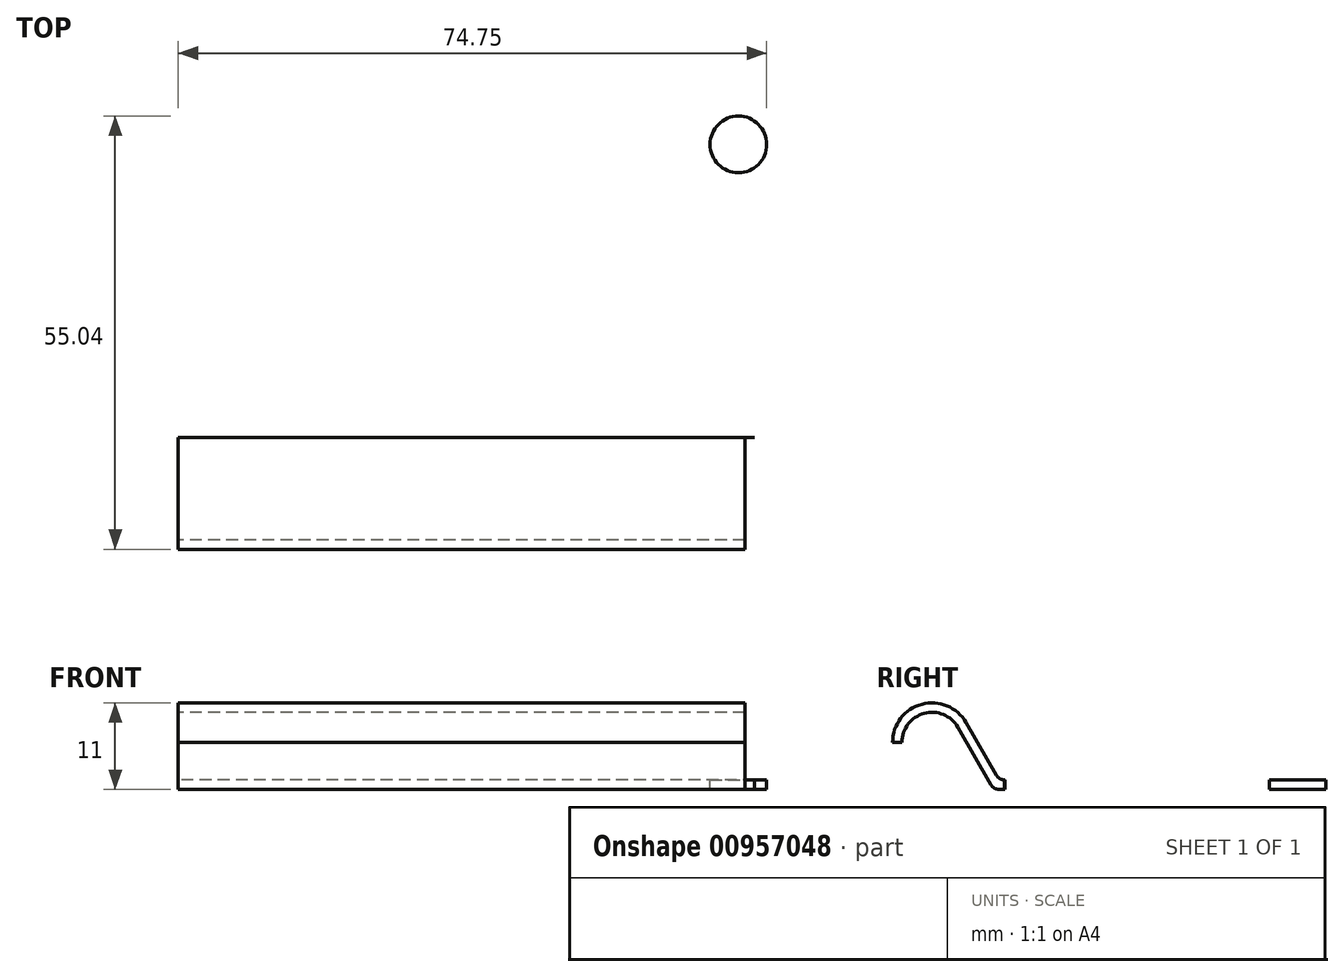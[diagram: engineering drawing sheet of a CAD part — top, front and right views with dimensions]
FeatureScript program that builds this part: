
annotation { "Feature Type Name" : "Feature", "Feature Type Description" : "" }
export const myFeature = defineFeature(function(context is Context, id is Id, definition is map)
    precondition{}
    {
        {
            var Q0;
            Q0=qCreatedBy(makeId("Right.planeOp"),FACE);
            var sketch = newSketch(context, id + "F0", { "sketchPlane" : qUnion([Q0])});
            skLineSegment(sketch, "E0.bottom", {"start": v(0, 0) * mm, "end": v(-46, 0) * mm});
            skLineSegment(sketch, "E0.top", {"start": v(0, 1.2) * mm, "end": v(-45.3, 1.2) * mm});
            skLineSegment(sketch, "E0.left", {"start": v(0, 0) * mm, "end": v(0, 1.2) * mm});
            skLineSegment(sketch, "E1", {"start": v(-55, 16.79) * mm, "end": v(-55, 2.5) * mm, "construction": true});
            skLineSegment(sketch, "E2", {"start": v(-55, 2.5) * mm, "end": v(-46.75, 2.5) * mm, "construction": true});
            skLineSegment(sketch, "E3", {"start": v(-46.35, 1.8) * mm, "end": v(-50.21, 8.5) * mm});
            skPoint(sketch, "E4.visualSharp", {"position": v(-46, 1.2) * mm});
            skArc(sketch, "E4.filletArc", {"start": v(-46.35, 1.8) * mm, "mid": v(-45.9, 1.36) * mm, "end": v(-45.3, 1.2) * mm});
            skLineSegment(sketch, "E5", {"start": v(-46, 0) * mm, "end": v(-44.99, 0) * mm});
            skPoint(sketch, "E6.visualSharp", {"position": v(-46.7, 0) * mm});
            skArc(sketch, "E6.filletArc", {"start": v(-47.04, 0.6) * mm, "mid": v(-46.6, 0.16) * mm, "end": v(-46, 0) * mm});
            skArc(sketch, "E7", {"start": v(-51.25, 7.9) * mm, "mid": v(-55.54, 9.67) * mm, "end": v(-58.34, 5.97) * mm});
            skArc(sketch, "E8", {"start": v(-50.21, 8.5) * mm, "mid": v(-55.85, 10.83) * mm, "end": v(-59.54, 5.97) * mm});
            skLineSegment(sketch, "E9", {"start": v(-59.54, 5.97) * mm, "end": v(-58.34, 5.97) * mm});
            skLineSegment(sketch, "E10.trimOffspring", {"start": v(-51.25, 7.9) * mm, "end": v(-47.04, 0.6) * mm});
            skSolve(sketch);
        }
        {
            var Q0;
            Q0 = qSketchRegion(id + "F0", true);
            extrude(context, id + "F1", {"entities" : qUnion([Q0]), "depth" : 136 * mm, "offsetDistance" : 25 * mm});
        }
        {
            var Q0;
            Q0=makeQuery(id+"F1.opExtrude","SWEPT_FACE",FACE,{"disambiguationData":[OSD([sQuery(id+"F0.wireOp",EDGE,"E0.top")])]});
            var sketch = newSketch(context, id + "F2", { "sketchPlane" : qUnion([Q0])});
            skCircle(sketch, "E11", {"center": v(32.85, -8.1) * mm, "radius": 3.6 * mm});
            skLineSegment(sketch, "E12", {"start": v(68, 0) * mm, "end": v(68, -66.92) * mm, "construction": true});
            skCircle(sketch, "E13.MirrorC", {"center": v(103.15, -8.1) * mm, "radius": 3.6 * mm});
            skLineSegment(sketch, "E14", {"start": v(145.84, -27) * mm, "end": v(-21.43, -27) * mm, "construction": true});
            skLineSegment(sketch, "E15", {"start": v(34.4, -45) * mm, "end": v(-31.77, -45) * mm, "construction": true});
            skLineSegment(sketch, "E16", {"start": v(0, -27) * mm, "end": v(34.83, -43.1) * mm});
            skLineSegment(sketch, "E17", {"start": v(40, -45) * mm, "end": v(0, -45) * mm});
            skLineSegment(sketch, "E18.MirrorCS", {"start": v(136, -27) * mm, "end": v(96.18, -45.4) * mm});
            skLineSegment(sketch, "E19", {"start": v(136.3, -27) * mm, "end": v(136, -45) * mm});
            skLineSegment(sketch, "E20", {"start": v(136, -45) * mm, "end": v(96.18, -45.4) * mm});
            skLineSegment(sketch, "E21", {"start": v(32, -66.59) * mm, "end": v(32, -45) * mm});
            skLineSegment(sketch, "E22", {"start": v(32, -45) * mm, "end": v(40, -45) * mm});
            skLineSegment(sketch, "E23", {"start": v(32, -60.73) * mm, "end": v(0, -60.73) * mm});
            skLineSegment(sketch, "E24", {"start": v(0, -60.73) * mm, "end": v(0, -27) * mm});
            skPoint(sketch, "E25.newPointB", {"position": v(39.82, -45.4) * mm});
            skArc(sketch, "E25.filletArc", {"start": v(34.4, -45) * mm, "mid": v(35.39, -44.21) * mm, "end": v(34.83, -43.1) * mm});
            skLineSegment(sketch, "E26.MirrorCS", {"start": v(104, -60.73) * mm, "end": v(136, -60.73) * mm});
            skLineSegment(sketch, "E27.MirrorCS", {"start": v(136, -60.73) * mm, "end": v(136, -27) * mm});
            skLineSegment(sketch, "E28.MirrorCS", {"start": v(104, -66.59) * mm, "end": v(104, -45) * mm});
            skLineSegment(sketch, "E29.MirrorCS", {"start": v(101.6, -45) * mm, "end": v(167.77, -45) * mm, "construction": true});
            skSolve(sketch);
        }
        {
            var Q0;
            Q0=makeQuery(id+"F2.imprint","IMPRINT",FACE,{"disambiguationData":[TD([[makeQuery(id+"F2.imprint","IMPRINT",EDGE,{"derivedFrom":sQuery(id+"F2.wireOp",EDGE,"E11")}),1.0]])]});
            var Q1;
            Q1=makeQuery(id+"F2.imprint","IMPRINT",FACE,{"disambiguationData":[TD([[makeQuery(id+"F2.imprint","IMPRINT",EDGE,{"derivedFrom":sQuery(id+"F2.wireOp",EDGE,"E13.MirrorC")}),-1.0]])]});
            var Q2;
            {var subQ4=sQuery(id+"F2.wireOp",EDGE,"E16");Q2=makeQuery(id+"F2.imprint","IMPRINT",FACE,{"disambiguationData":[TD([[makeQuery(id+"F2.imprint","IMPRINT",EDGE,{"derivedFrom":subQ4}),-1.0]])]});}
            var Q3;
            {var subQ0=sQuery(id+"F2.wireOp",EDGE,"E17");Q3=makeQuery(id+"F2.imprint","IMPRINT",FACE,{"disambiguationData":[TD([[makeQuery(id+"F2.imprint","IMPRINT",EDGE,{"derivedFrom":subQ0}),1.0]])]});}
            var Q4;
            {var subQ0=sQuery(id+"F2.wireOp",EDGE,"E23");Q4=makeQuery(id+"F2.imprint","IMPRINT",FACE,{"disambiguationData":[TD([[makeQuery(id+"F2.imprint","IMPRINT",EDGE,{"derivedFrom":subQ0}),-1.0]])]});}
            var Q5;
            {var subQ1=sQuery(id+"F2.wireOp",EDGE,"E26.MirrorCS");Q5=makeQuery(id+"F2.imprint","IMPRINT",FACE,{"disambiguationData":[TD([[makeQuery(id+"F2.imprint","IMPRINT",EDGE,{"derivedFrom":subQ1}),1.0]])]});}
            var Q6;
            {var subQ0=sQuery(id+"F2.wireOp",EDGE,"E27.MirrorCS");var subQ1=sQuery(id+"F2.wireOp",EDGE,"E20");var subQ2=makeQuery(id+"F2.imprint","INTERSECT",VERTEX,{"derivedFrom":[subQ1,subQ0]});Q6=makeQuery(id+"F2.imprint","IMPRINT",FACE,{"disambiguationData":[TD([[makeQuery(id+"F2.imprint","IMPRINT",EDGE,{"disambiguationData":[TD([[subQ2,-1.0]])],"derivedFrom":subQ1}),-1.0]])]});}
            var Q7;
            {var subQ0=sQuery(id+"F2.wireOp",EDGE,"E27.MirrorCS");var subQ1=sQuery(id+"F2.wireOp",EDGE,"E20");var subQ2=makeQuery(id+"F2.imprint","INTERSECT",VERTEX,{"derivedFrom":[subQ1,subQ0]});Q7=makeQuery(id+"F2.imprint","IMPRINT",FACE,{"disambiguationData":[TD([[makeQuery(id+"F2.imprint","IMPRINT",EDGE,{"disambiguationData":[TD([[subQ2,-1.0]])],"derivedFrom":subQ1}),1.0]])]});}
            extrude(context, id + "F3", {"entities" : qUnion([Q0, Q1, Q2, Q3, Q4, Q5, Q6, Q7]), "operationType" : NewBodyOperationType.REMOVE, "oppositeDirection" : true, "depth" : 25 * mm, "offsetDistance" : 25 * mm, "hasSecondDirection" : true, "secondDirectionOppositeDirection" : false, "secondDirectionDepth" : 25 * mm});
        }
    });
